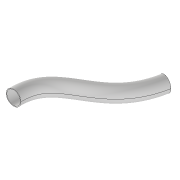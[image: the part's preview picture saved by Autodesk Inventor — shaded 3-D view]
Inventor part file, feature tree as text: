
AUTODESK INVENTOR PART (.ipt)
format: ipt  version: 2020 (Build 240168000, 168)  size: 278,016 bytes
history: native  units: mm
features: sketch x2, sweep x1
ambient origin geometry x8: Origin, YZ Plane, XZ Plane, XY Plane, X Axis, Y Axis, Z Axis, Center Point
bodies: Volumenkörper1 (feature_tree)
feature tree (3):
  sweep  "Sweeping1"
  sketch  "Skizze1"  dims[d0=100.0mm d1=110.0mm]
  sketch  "Skizze2"  dims[d2=0.0mm d3=0.0mm]
